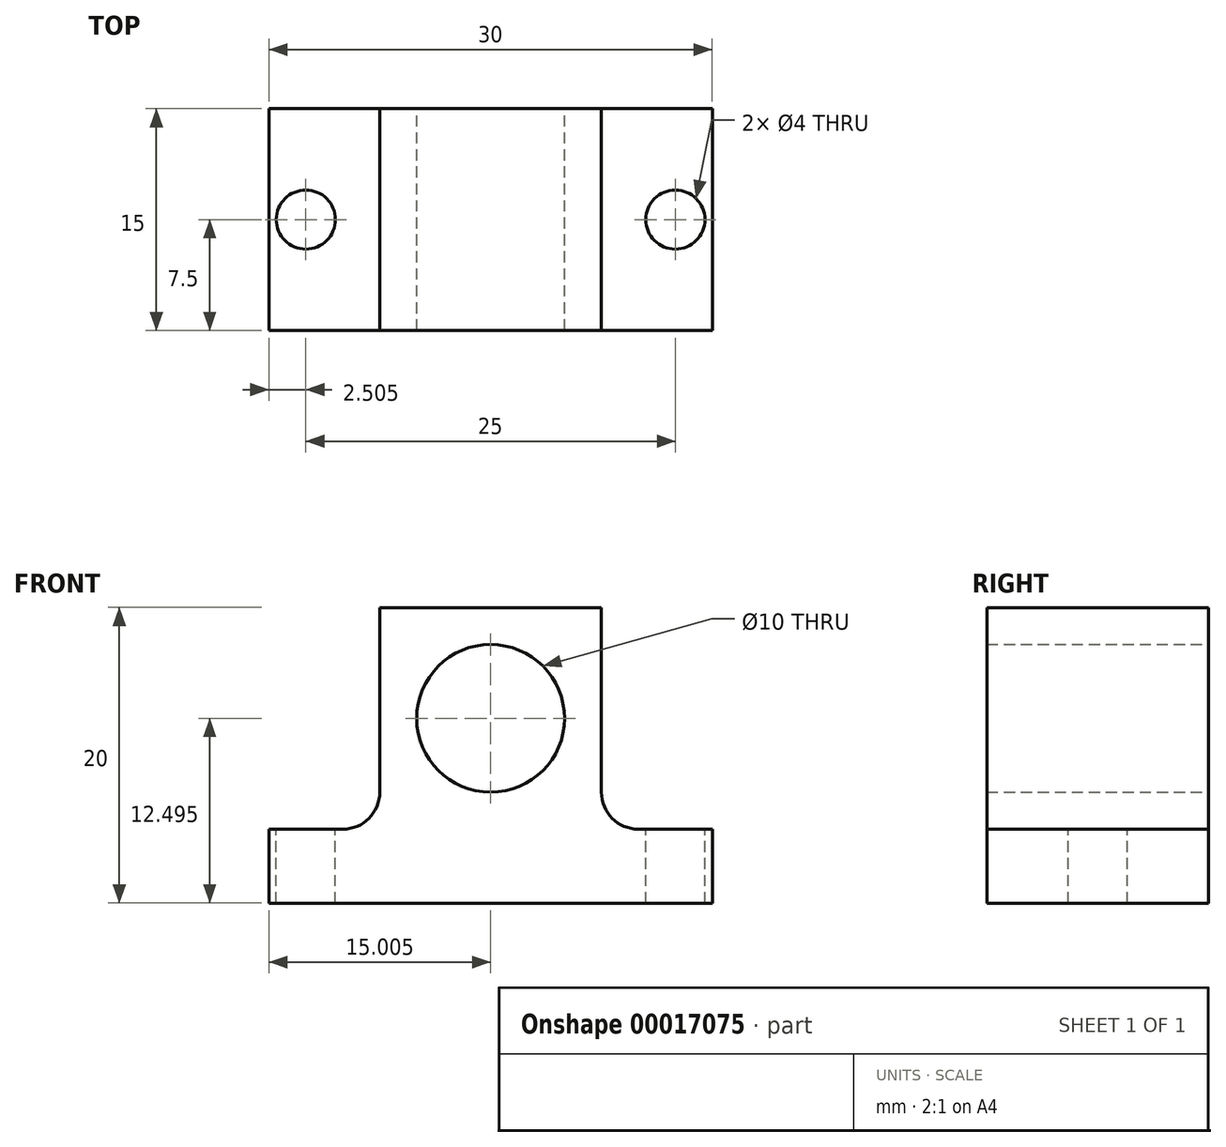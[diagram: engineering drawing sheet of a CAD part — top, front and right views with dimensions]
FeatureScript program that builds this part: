
annotation { "Feature Type Name" : "Feature", "Feature Type Description" : "" }
export const myFeature = defineFeature(function(context is Context, id is Id, definition is map)
    precondition{}
    {
        {
            var Q0;
            Q0=qCreatedBy(makeId("Front.planeOp"),FACE);
            var sketch = newSketch(context, id + "F0", { "sketchPlane" : qUnion([Q0])});
            skLineSegment(sketch, "E0", {"start": v(-47.2, -12.38) * mm, "end": v(-47.2, -17.38) * mm});
            skLineSegment(sketch, "E1", {"start": v(-47.2, -17.38) * mm, "end": v(-17.2, -17.38) * mm});
            skLineSegment(sketch, "E2", {"start": v(-17.2, -17.38) * mm, "end": v(-17.2, -12.38) * mm});
            skLineSegment(sketch, "E3", {"start": v(-17.2, -12.38) * mm, "end": v(-22.2, -12.38) * mm});
            skLineSegment(sketch, "E4", {"start": v(-24.7, -9.88) * mm, "end": v(-24.7, 2.62) * mm});
            skLineSegment(sketch, "E5", {"start": v(-24.7, 2.62) * mm, "end": v(-39.7, 2.62) * mm});
            skLineSegment(sketch, "E6", {"start": v(-39.7, 2.62) * mm, "end": v(-39.7, -9.88) * mm});
            skLineSegment(sketch, "E7", {"start": v(-42.2, -12.38) * mm, "end": v(-47.2, -12.38) * mm});
            skPoint(sketch, "E8.visualSharp", {"position": v(-39.7, -12.38) * mm});
            skArc(sketch, "E8.filletArc", {"start": v(-42.2, -12.38) * mm, "mid": v(-40.44, -11.65) * mm, "end": v(-39.7, -9.88) * mm});
            skPoint(sketch, "E9.visualSharp", {"position": v(-24.7, -12.38) * mm});
            skArc(sketch, "E9.filletArc", {"start": v(-24.7, -9.88) * mm, "mid": v(-23.97, -11.65) * mm, "end": v(-22.2, -12.38) * mm});
            skCircle(sketch, "E10", {"center": v(-32.2, -4.88) * mm, "radius": 5 * mm});
            skSolve(sketch);
        }
        {
            var Q0;
            Q0=makeQuery(id+"F0.imprint","IMPRINT",FACE,{"disambiguationData":[TD([[makeQuery(id+"F0.imprint","IMPRINT",EDGE,{"derivedFrom":sQuery(id+"F0.wireOp",EDGE,"E0")}),1.0]])]});
            extrude(context, id + "F1", {"entities" : qUnion([Q0]), "depth" : 15 * mm});
        }
        {
            var Q0;
            Q0=makeQuery(id+"F1.opExtrude","SWEPT_FACE",FACE,{"disambiguationData":[OSD([sQuery(id+"F0.wireOp",EDGE,"E7")])]});
            var sketch = newSketch(context, id + "F2", { "sketchPlane" : qUnion([Q0])});
            skLineSegment(sketch, "E11", {"start": v(-42.2, 0) * mm, "end": v(-47.2, 0) * mm});
            skCircle(sketch, "E12", {"center": v(-44.7, -7.5) * mm, "radius": 2 * mm});
            skSolve(sketch);
        }
        {
            var Q0;
            Q0=makeQuery(id+"F1.opExtrude","SWEPT_FACE",FACE,{"disambiguationData":[OSD([sQuery(id+"F0.wireOp",EDGE,"E3")])]});
            var sketch = newSketch(context, id + "F3", { "sketchPlane" : qUnion([Q0])});
            skLineSegment(sketch, "E13", {"start": v(-17.2, 0) * mm, "end": v(-22.2, 0) * mm});
            skCircle(sketch, "E14", {"center": v(-19.7, -7.5) * mm, "radius": 2 * mm});
            skSolve(sketch);
        }
        {
            var Q0;
            Q0=makeQuery(id+"F3.imprint","IMPRINT",FACE,{"disambiguationData":[TD([[makeQuery(id+"F3.imprint","IMPRINT",EDGE,{"derivedFrom":sQuery(id+"F3.wireOp",EDGE,"E14")}),1.0]])]});
            var Q1;
            Q1=makeQuery(id+"F2.imprint","IMPRINT",FACE,{"disambiguationData":[TD([[makeQuery(id+"F2.imprint","IMPRINT",EDGE,{"derivedFrom":sQuery(id+"F2.wireOp",EDGE,"E12")}),1.0]])]});
            extrude(context, id + "F4", {"entities" : qUnion([Q0, Q1]), "operationType" : NewBodyOperationType.REMOVE, "endBound" : BoundingType.THROUGH_ALL, "oppositeDirection" : true, "depth" : 25 * mm});
        }
    });
